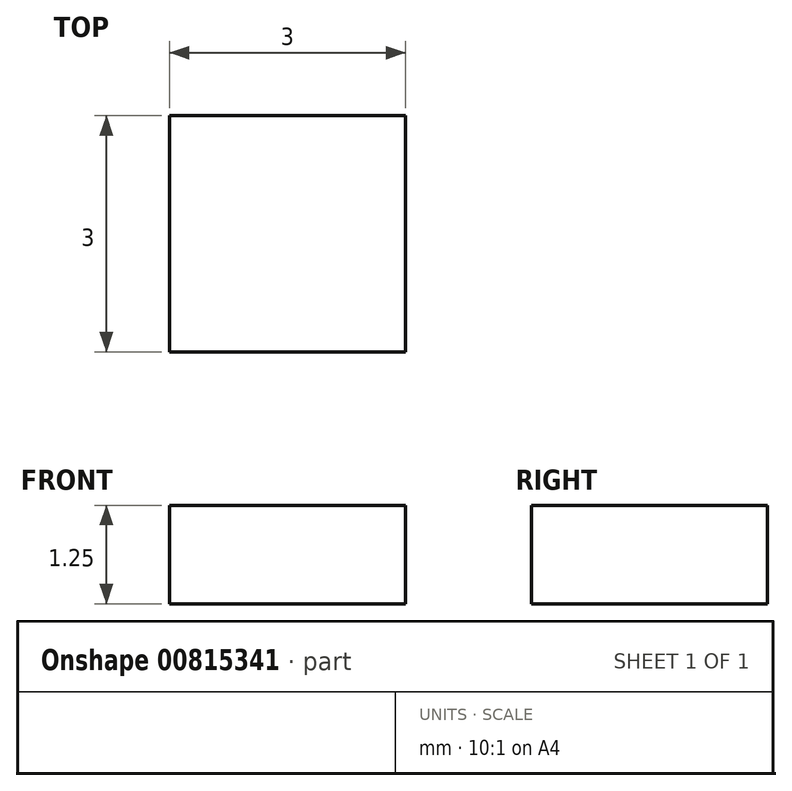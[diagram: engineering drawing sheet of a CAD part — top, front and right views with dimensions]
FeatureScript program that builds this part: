
annotation { "Feature Type Name" : "Feature", "Feature Type Description" : "" }
export const myFeature = defineFeature(function(context is Context, id is Id, definition is map)
    precondition{}
    {
        {
            var Q0;
            Q0=qCreatedBy(makeId("Top.planeOp"),FACE);
            var sketch = newSketch(context, id + "F0", { "sketchPlane" : qUnion([Q0])});
            skLineSegment(sketch, "E0.bottom", {"start": v(0, 0) * mm, "end": v(3, 0) * mm});
            skLineSegment(sketch, "E0.top", {"start": v(0, -3) * mm, "end": v(3, -3) * mm});
            skLineSegment(sketch, "E0.left", {"start": v(0, 0) * mm, "end": v(0, -3) * mm});
            skLineSegment(sketch, "E0.right", {"start": v(3, 0) * mm, "end": v(3, -3) * mm});
            skSolve(sketch);
        }
        {
            var Q0;
            Q0=makeQuery(id+"F0.imprint","IMPRINT",FACE,{"disambiguationData":[TD([[makeQuery(id+"F0.imprint","IMPRINT",EDGE,{"derivedFrom":sQuery(id+"F0.wireOp",EDGE,"E0.bottom")}),-1.0]])]});
            extrude(context, id + "F1", {"entities" : qUnion([Q0]), "depth" : 1.25 * mm, "offsetDistance" : 25 * mm});
        }
    });
